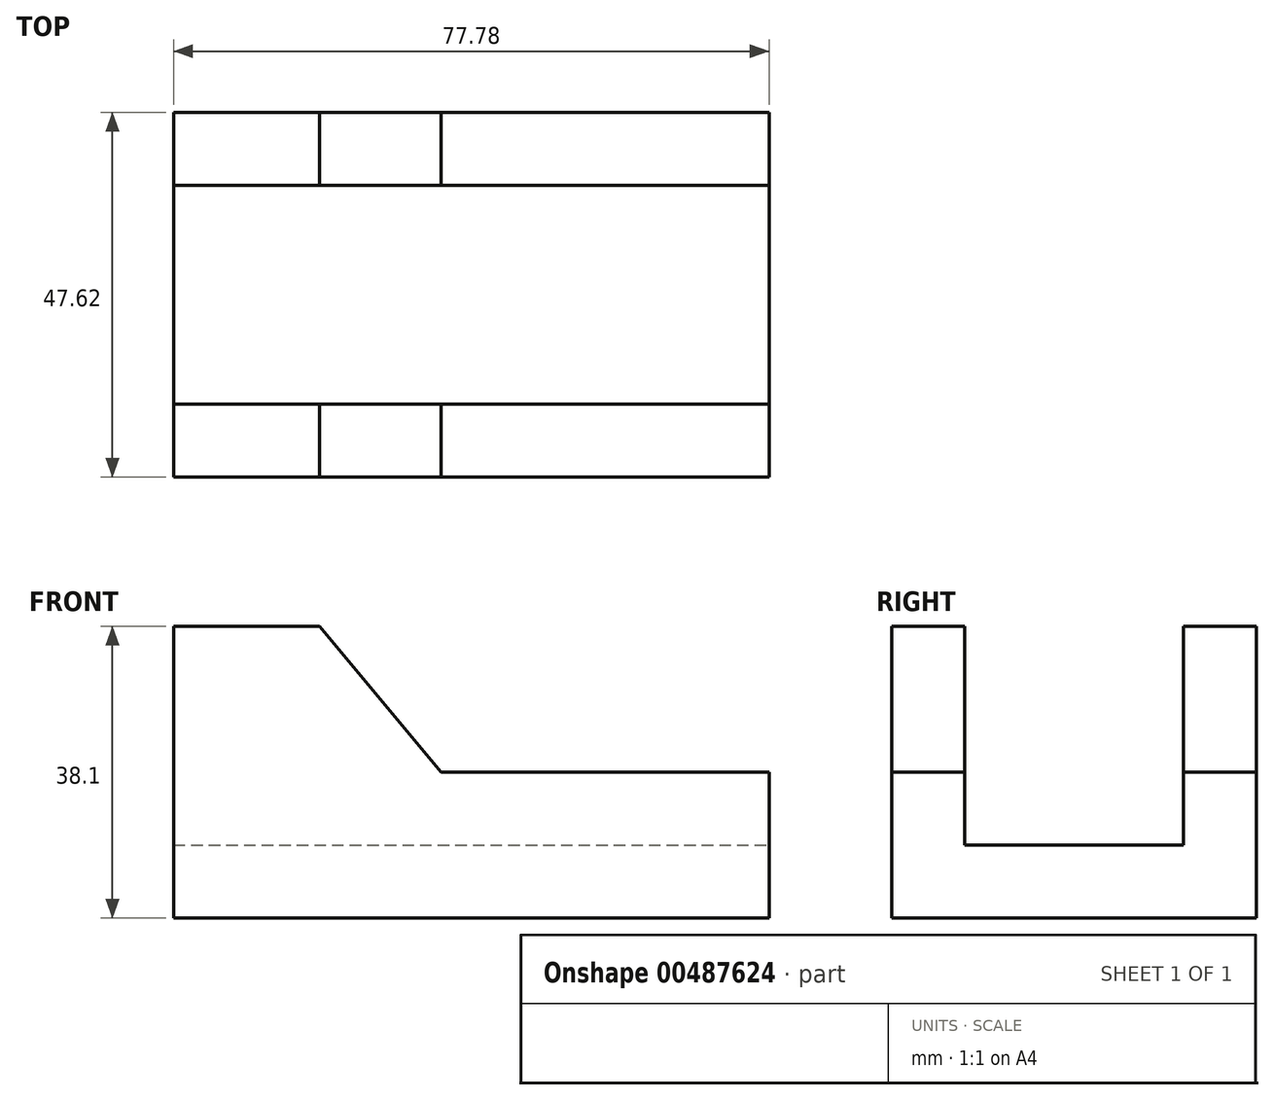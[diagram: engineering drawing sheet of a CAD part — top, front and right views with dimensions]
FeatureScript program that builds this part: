
annotation { "Feature Type Name" : "Feature", "Feature Type Description" : "" }
export const myFeature = defineFeature(function(context is Context, id is Id, definition is map)
    precondition{}
    {
        {
            var Q0;
            Q0=qCreatedBy(makeId("Top.planeOp"),FACE);
            var sketch = newSketch(context, id + "F0", { "sketchPlane" : qUnion([Q0])});
            skLineSegment(sketch, "E0.bottom", {"start": v(-38.9, 23.81) * mm, "end": v(38.9, 23.81) * mm});
            skLineSegment(sketch, "E0.top", {"start": v(-38.9, -23.81) * mm, "end": v(38.9, -23.81) * mm});
            skLineSegment(sketch, "E0.left", {"start": v(-38.9, 23.81) * mm, "end": v(-38.9, -23.81) * mm});
            skLineSegment(sketch, "E0.right", {"start": v(38.9, 23.81) * mm, "end": v(38.9, -23.81) * mm});
            skPoint(sketch, "E0.middle", {"position": v(0, 0) * mm});
            skSolve(sketch);
        }
        {
            var Q0;
            Q0=makeQuery(id+"F0.imprint","IMPRINT",FACE,{"disambiguationData":[TD([[makeQuery(id+"F0.imprint","IMPRINT",EDGE,{"derivedFrom":sQuery(id+"F0.wireOp",EDGE,"E0.bottom")}),-1.0]])]});
            extrude(context, id + "F1", {"entities" : qUnion([Q0]), "depth" : 9.52 * mm});
        }
        {
            var Q0;
            Q0=makeQuery(id+"F1.opExtrude","SWEPT_FACE",FACE,{"disambiguationData":[OSD([sQuery(id+"F0.wireOp",EDGE,"E0.top")])]});
            var sketch = newSketch(context, id + "F2", { "sketchPlane" : qUnion([Q0])});
            skLineSegment(sketch, "E1", {"start": v(-38.9, 0) * mm, "end": v(-38.9, 38.1) * mm});
            skLineSegment(sketch, "E2", {"start": v(-3.97, 19.05) * mm, "end": v(38.9, 19.05) * mm});
            skLineSegment(sketch, "E3", {"start": v(38.9, 19.05) * mm, "end": v(38.9, 0) * mm});
            skLineSegment(sketch, "E4", {"start": v(-38.9, 38.1) * mm, "end": v(-19.84, 38.1) * mm});
            skLineSegment(sketch, "E5", {"start": v(-19.84, 38.1) * mm, "end": v(-3.97, 19.05) * mm});
            skSolve(sketch);
        }
        {
            var Q0;
            {var subQ2=sQuery(id+"F2.wireOp",EDGE,"E2");Q0=makeQuery(id+"F2.imprint","IMPRINT",FACE,{"disambiguationData":[TD([[makeQuery(id+"F2.imprint","IMPRINT",EDGE,{"derivedFrom":subQ2}),-1.0]])]});}
            extrude(context, id + "F3", {"entities" : qUnion([Q0]), "operationType" : NewBodyOperationType.ADD, "oppositeDirection" : true, "depth" : 9.52 * mm});
        }
        {
            var Q0;
            Q0=makeQuery(id+"F1.opExtrude","SWEPT_BODY",BODY,{"disambiguationData":[OSD([sQuery(id+"F0.wireOp",EDGE,"E0.bottom"),sQuery(id+"F0.wireOp",EDGE,"E0.top"),sQuery(id+"F0.wireOp",EDGE,"E0.left"),sQuery(id+"F0.wireOp",EDGE,"E0.right")])]});
            var Q1;
            Q1=qCreatedBy(makeId("Front.planeOp"),FACE);
            mirror(context, id + "F4", {"operationType" : NewBodyOperationType.ADD, "entities" : qUnion([Q0]), "mirrorPlane" : qUnion([Q1])});
        }
    });
